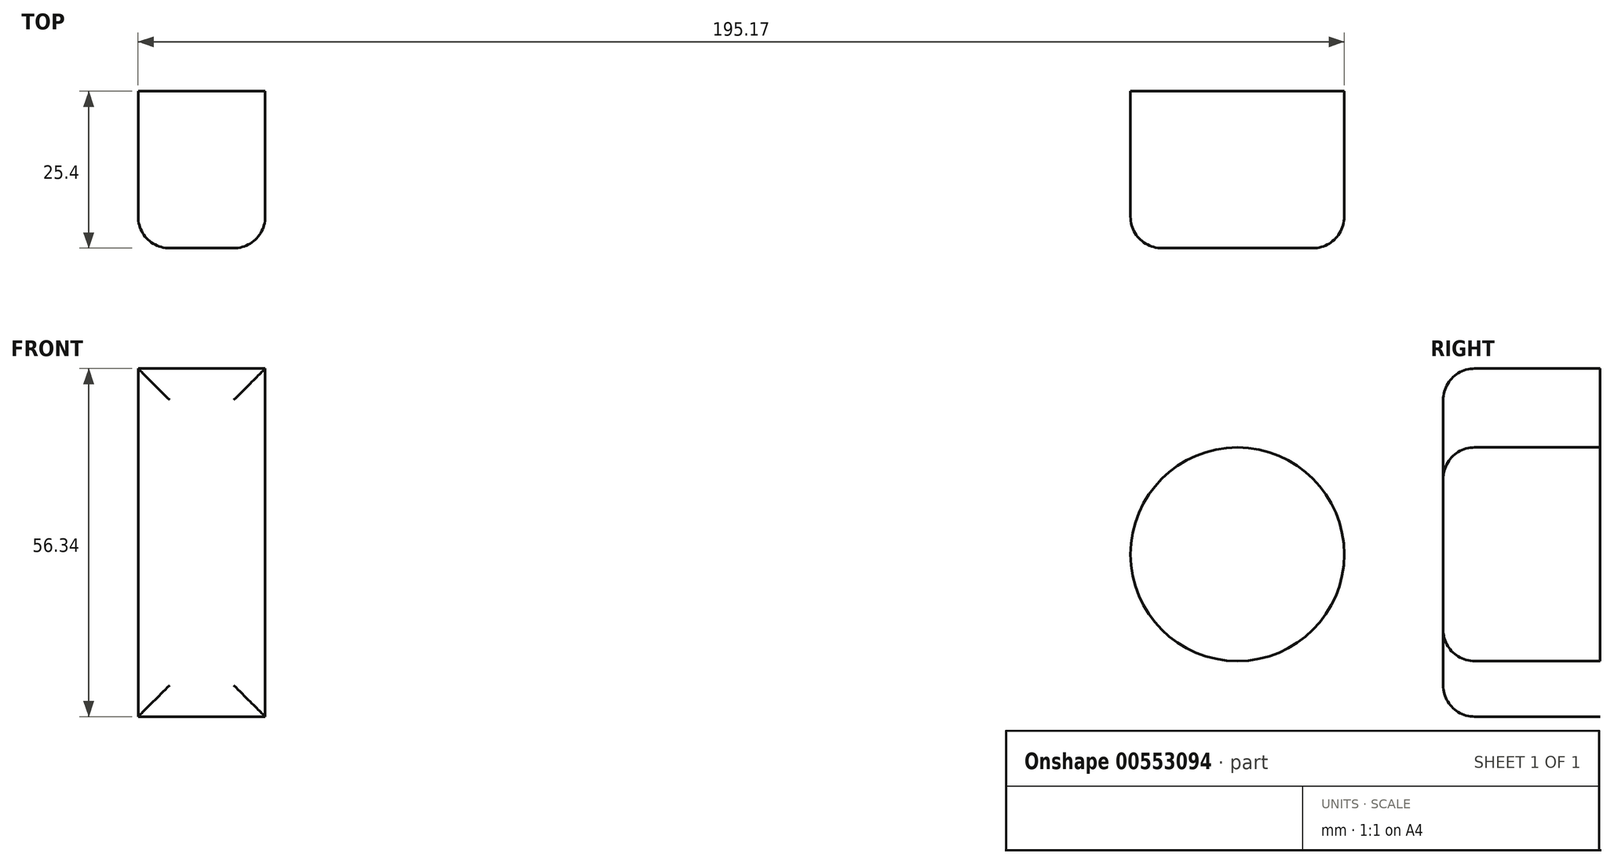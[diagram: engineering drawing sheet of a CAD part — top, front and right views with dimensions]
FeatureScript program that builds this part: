
annotation { "Feature Type Name" : "Feature", "Feature Type Description" : "" }
export const myFeature = defineFeature(function(context is Context, id is Id, definition is map)
    precondition{}
    {
        {
            var Q0;
            Q0=qCreatedBy(makeId("Front.planeOp"),FACE);
            var sketch = newSketch(context, id + "F0", { "sketchPlane" : qUnion([Q0])});
            skLineSegment(sketch, "E0.bottom", {"start": v(-106.9, 52.28) * mm, "end": v(-86.33, 52.28) * mm});
            skLineSegment(sketch, "E0.top", {"start": v(-106.9, -4.06) * mm, "end": v(-86.33, -4.06) * mm});
            skLineSegment(sketch, "E0.left", {"start": v(-106.9, 52.28) * mm, "end": v(-106.9, -4.06) * mm});
            skLineSegment(sketch, "E0.right", {"start": v(-86.33, 52.28) * mm, "end": v(-86.33, -4.06) * mm});
            skCircle(sketch, "E1", {"center": v(70.98, 22.23) * mm, "radius": 17.29 * mm});
            skSolve(sketch);
        }
        {
            var Q0;
            Q0 = qSketchRegion(id + "F0", true);
            extrude(context, id + "F1", {"entities" : qUnion([Q0]), "depth" : 25.4 * mm, "offsetDistance" : 25.4 * mm});
        }
        {
            var Q0;
            Q0=makeQuery(id+"F1.opExtrude","CAP_FACE",FACE,{"disambiguationData":[OSD([sQuery(id+"F0.wireOp",EDGE,"E0.bottom"),sQuery(id+"F0.wireOp",EDGE,"E0.top"),sQuery(id+"F0.wireOp",EDGE,"E0.left"),sQuery(id+"F0.wireOp",EDGE,"E0.right")])],"isStart":false});
            var Q1;
            Q1=makeQuery(id+"F1.opExtrude","CAP_FACE",FACE,{"disambiguationData":[OSD([sQuery(id+"F0.wireOp",EDGE,"E1")])],"isStart":false});
            fillet(context, id + "F2", {"entities" : qUnion([Q0, Q1]), "radius" : 5.08 * mm, "tangentPropagation" : true, "allowEdgeOverflow" : false});
        }
    });
